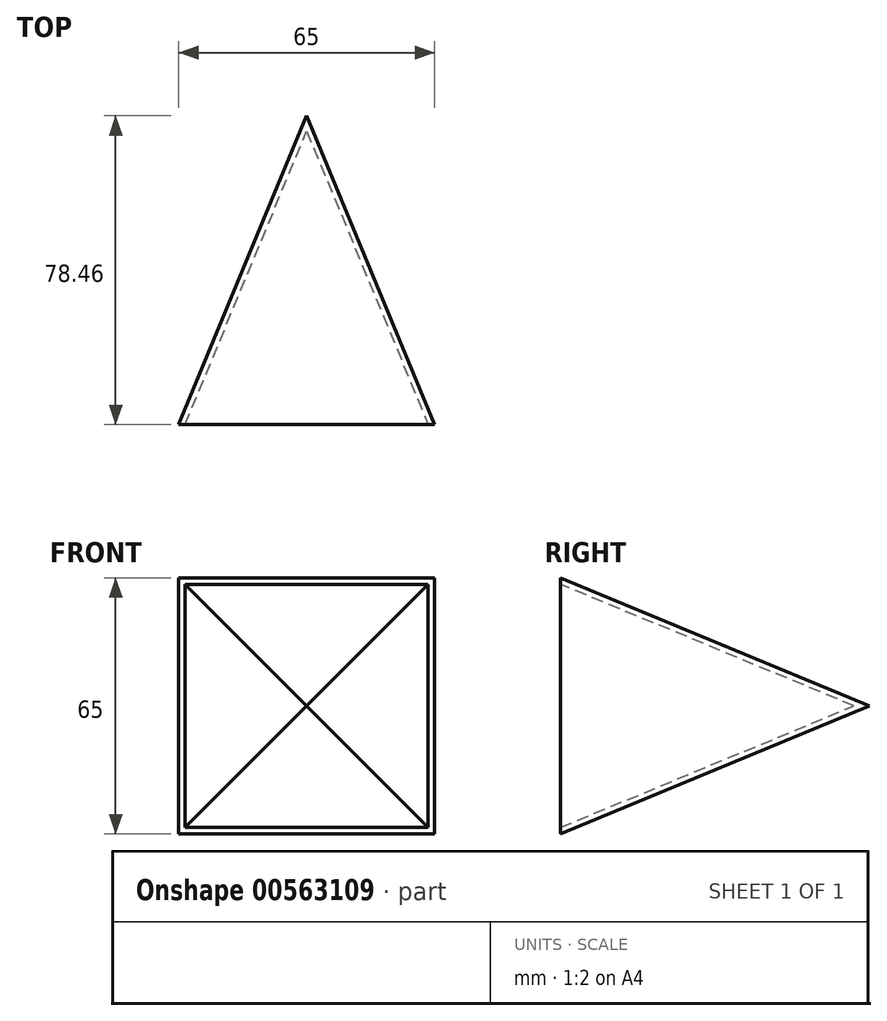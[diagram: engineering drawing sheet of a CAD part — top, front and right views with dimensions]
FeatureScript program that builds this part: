
annotation { "Feature Type Name" : "Feature", "Feature Type Description" : "" }
export const myFeature = defineFeature(function(context is Context, id is Id, definition is map)
    precondition{}
    {
        {
            var Q0;
            Q0=qCreatedBy(makeId("Front.planeOp"),FACE);
            var sketch = newSketch(context, id + "F0", { "sketchPlane" : qUnion([Q0])});
            skLineSegment(sketch, "E0.bottom", {"start": v(0, 0) * mm, "end": v(65, 0) * mm});
            skLineSegment(sketch, "E0.top", {"start": v(0, 65) * mm, "end": v(65, 65) * mm});
            skLineSegment(sketch, "E0.left", {"start": v(0, 0) * mm, "end": v(0, 65) * mm});
            skLineSegment(sketch, "E0.right", {"start": v(65, 0) * mm, "end": v(65, 65) * mm});
            skLineSegment(sketch, "E1", {"start": v(0, 0) * mm, "end": v(1.5, 0) * mm, "construction": true});
            skLineSegment(sketch, "E2", {"start": v(1.5, 0) * mm, "end": v(1.5, 1.5) * mm, "construction": true});
            skLineSegment(sketch, "E3.bottom", {"start": v(1.5, 1.5) * mm, "end": v(63.5, 1.5) * mm});
            skLineSegment(sketch, "E3.top", {"start": v(1.5, 63.5) * mm, "end": v(63.5, 63.5) * mm});
            skLineSegment(sketch, "E3.left", {"start": v(1.5, 1.5) * mm, "end": v(1.5, 63.5) * mm});
            skLineSegment(sketch, "E3.right", {"start": v(63.5, 1.5) * mm, "end": v(63.5, 63.5) * mm});
            skSolve(sketch);
        }
        {
            var Q0;
            Q0=makeQuery(id+"F0.imprint","IMPRINT",FACE,{"disambiguationData":[TD([[makeQuery(id+"F0.imprint","IMPRINT",EDGE,{"derivedFrom":sQuery(id+"F0.wireOp",EDGE,"E0.bottom")}),1.0]])]});
            var Q1;
            Q1=makeQuery(id+"F0.imprint","IMPRINT",FACE,{"disambiguationData":[TD([[makeQuery(id+"F0.imprint","IMPRINT",EDGE,{"derivedFrom":sQuery(id+"F0.wireOp",EDGE,"E3.bottom")}),1.0]])]});
            extrude(context, id + "F1", {"entities" : qUnion([Q0, Q1]), "oppositeDirection" : true, "depth" : 80 * mm, "offsetDistance" : 25 * mm, "hasDraft" : true, "draftAngle" : 22.5 * degree, "draftPullDirection" : true});
        }
        {
            var Q0;
            Q0=makeQuery(id+"F1.opExtrude","CAP_FACE",FACE,{"disambiguationData":[OSD([sQuery(id+"F0.wireOp",EDGE,"E0.bottom"),sQuery(id+"F0.wireOp",EDGE,"E0.top"),sQuery(id+"F0.wireOp",EDGE,"E0.left"),sQuery(id+"F0.wireOp",EDGE,"E0.right")])],"isStart":true});
            shell(context, id + "F2", {"entities" : qUnion([Q0]), "thickness" : 1.5 * mm});
        }
    });
